# Revit family: Mailboxes_Americana-Salsbury_Industries-Rear_Loading
name_source: partatom
category: Specialty Equipment
revit_build: Autodesk Revit 2016 (Build: 20150714_1515(x64)
units: mm (PartAtom-declared; Revit-internal decimal feet)

## family parameters
Always vertical = Yes
Cut with Voids When Loaded = No
OmniClass Number = 23.40.90.14.11
OmniClass Title = Mail Boxes
Part Type = Normal
Room Calculation Point = No
Round Connector Dimension = Use Diameter
Shared = No
Work Plane-Based = No

## types (4) — shared parameters
Assembly Code = C1030910
Depth = 14.875 "
Door Material = Brass Die Cast - Salsbury Finish - Brass
Door Material - Textured = Brass Die Cast - Salsbury Finish - Textured
Door Window Material = Glass - Salsbury Finish - Clear
Enclosure Material = Steel - Salsbury Finish - Tan
Height = 26.375 "
Lock Material = Stainless Steel - Salsbury Finish - Gold
Manufacturer = Salsbury Industries
MasterFormat Number = 10 55 00
MasterFormat Title = Postal Specialties
Name Plate Material = Aluminum - Salsbury Finish -  Brushed Steel
Name Plate Offset = 0.032 "
OmniClass 23 Title = Mail Boxes
OmniClass23 Number = 23.40.90.14.11
Type Comments = Brass Mailbox for Private Delivery
URL = www.mailboxes.com
Version = 2.0 (05/31/18)
Width = 23.5 "
zero-valued in all types: Door Offset for Front Loading Units

## per-type parameters (varying)
- 2016RL: Description=Rear-Loading Unit with 16 #2 Doors; Divider 6 and 7 Offset=0 "; Door Slot L1=Brass Mailbox No Door : Empty; Door Slot L1-A=Brass Mailbox #2 Door : #2 Door; Door Slot L10=Brass Mailbox No Door : Empty; Door Slot L10-A=Brass Mailbox #2 Door : #2 Door; Door Slot L11=Brass Mailbox No Door : Empty; Door Slot L11-A=Brass Mailbox #2 Door : #2 Door; Door Slot L12=Brass Mailbox No Door : Empty; Door Slot L12-A=Brass Mailbox #2 Door : #2 Door; Door Slot L13=Brass Mailbox No Door : Empty; Door Slot L13-A=Brass Mailbox #2 Door : #2 Door; Door Slot L14=Brass Mailbox No Door : Empty; Door Slot L14-A=Brass Mailbox #2 Door : #2 Door; Door Slot L15=Brass Mailbox No Door : Empty; Door Slot L15-A=Brass Mailbox #2 Door : #2 Door; Door Slot L16=Brass Mailbox No Door : Empty; Door Slot L16-A=Brass Mailbox #2 Door : #2 Door; Door Slot L17=Brass Mailbox No Door : Empty; Door Slot L18=Brass Mailbox No Door : Empty; Door Slot L19=Brass Mailbox No Door : Empty; Door Slot L2=Brass Mailbox No Door : Empty; Door Slot L2-A=Brass Mailbox #2 Door : #2 Door; Door Slot L20=Brass Mailbox No Door : Empty; Door Slot L21=Brass Mailbox No Door : Empty; Door Slot L22=Brass Mailbox No Door : Empty; Door Slot L23=Brass Mailbox No Door : Empty; Door Slot L24=Brass Mailbox No Door : Empty; Door Slot L25=Brass Mailbox No Door : Empty; Door Slot L26=Brass Mailbox No Door : Empty; Door Slot L27=Brass Mailbox No Door : Empty; Door Slot L28=Brass Mailbox No Door : Empty; Door Slot L29=Brass Mailbox No Door : Empty; Door Slot L3=Brass Mailbox No Door : Empty; Door Slot L3-A=Brass Mailbox #2 Door : #2 Door; Door Slot L30=Brass Mailbox No Door : Empty; Door Slot L4=Brass Mailbox No Door : Empty; Door Slot L4-A=Brass Mailbox #2 Door : #2 Door; Door Slot L5=Brass Mailbox No Door : Empty; Door Slot L5-A=Brass Mailbox #2 Door : #2 Door; Door Slot L6=Brass Mailbox No Door : Empty; Door Slot L6-A=Brass Mailbox #2 Door : #2 Door; Door Slot L7=Brass Mailbox No Door : Empty; Door Slot L7-A=Brass Mailbox #2 Door : #2 Door; Door Slot L8=Brass Mailbox No Door : Empty; Door Slot L8-A=Brass Mailbox #2 Door : #2 Door; Door Slot L9=Brass Mailbox No Door : Empty; Door Slot L9-A=Brass Mailbox #2 Door : #2 Door; Horizontal Dividers 1, 2, 3, 4=No; Horizontal Dividers 5, 6, 7=Yes; Vertical Dividers 1, 2, 4, 5=No; Vertical Dividers 6, 7=Yes
- 2030RL: Description=Rear-Loading Unit with 30 #1 Doors; Divider 6 and 7 Offset=0 "; Door Slot L1=Brass Mailbox #1 Door : #1 Door; Door Slot L1-A=Brass Mailbox No Door : Empty; Door Slot L10=Brass Mailbox #1 Door : #1 Door; Door Slot L10-A=Brass Mailbox No Door : Empty; Door Slot L11=Brass Mailbox #1 Door : #1 Door; Door Slot L11-A=Brass Mailbox No Door : Empty; Door Slot L12=Brass Mailbox #1 Door : #1 Door; Door Slot L12-A=Brass Mailbox No Door : Empty; Door Slot L13=Brass Mailbox #1 Door : #1 Door; Door Slot L13-A=Brass Mailbox No Door : Empty; Door Slot L14=Brass Mailbox #1 Door : #1 Door; Door Slot L14-A=Brass Mailbox No Door : Empty; Door Slot L15=Brass Mailbox #1 Door : #1 Door; Door Slot L15-A=Brass Mailbox No Door : Empty; Door Slot L16=Brass Mailbox #1 Door : #1 Door; Door Slot L16-A=Brass Mailbox No Door : Empty; Door Slot L17=Brass Mailbox #1 Door : #1 Door; Door Slot L18=Brass Mailbox #1 Door : #1 Door; Door Slot L19=Brass Mailbox #1 Door : #1 Door; Door Slot L2=Brass Mailbox #1 Door : #1 Door; Door Slot L2-A=Brass Mailbox No Door : Empty; Door Slot L20=Brass Mailbox #1 Door : #1 Door; Door Slot L21=Brass Mailbox #1 Door : #1 Door; Door Slot L22=Brass Mailbox #1 Door : #1 Door; Door Slot L23=Brass Mailbox #1 Door : #1 Door; Door Slot L24=Brass Mailbox #1 Door : #1 Door; Door Slot L25=Brass Mailbox #1 Door : #1 Door; Door Slot L26=Brass Mailbox #1 Door : #1 Door; Door Slot L27=Brass Mailbox #1 Door : #1 Door; Door Slot L28=Brass Mailbox #1 Door : #1 Door; Door Slot L29=Brass Mailbox #1 Door : #1 Door; Door Slot L3=Brass Mailbox #1 Door : #1 Door; Door Slot L3-A=Brass Mailbox No Door : Empty; Door Slot L30=Brass Mailbox #1 Door : #1 Door; Door Slot L4=Brass Mailbox #1 Door : #1 Door; Door Slot L4-A=Brass Mailbox No Door : Empty; Door Slot L5=Brass Mailbox #1 Door : #1 Door; Door Slot L5-A=Brass Mailbox No Door : Empty; Door Slot L6=Brass Mailbox #1 Door : #1 Door; Door Slot L6-A=Brass Mailbox No Door : Empty; Door Slot L7=Brass Mailbox #1 Door : #1 Door; Door Slot L7-A=Brass Mailbox No Door : Empty; Door Slot L8=Brass Mailbox #1 Door : #1 Door; Door Slot L8-A=Brass Mailbox No Door : Empty; Door Slot L9=Brass Mailbox #1 Door : #1 Door; Door Slot L9-A=Brass Mailbox No Door : Empty; Horizontal Dividers 1, 2, 3, 4=Yes; Horizontal Dividers 5, 6, 7=No; Vertical Dividers 1, 2, 4, 5=Yes; Vertical Dividers 6, 7=No
- 2014RL: Description=Rear-Loading Unit with 14 #2 Doors, 2 #3 Doors; Divider 6 and 7 Offset=6.577 "; Door Slot L1=Brass Mailbox No Door : Empty; Door Slot L1-A=Brass Mailbox #2 Door : #2 Door; Door Slot L10=Brass Mailbox No Door : Empty; Door Slot L10-A=Brass Mailbox #2 Door : #2 Door; Door Slot L11=Brass Mailbox No Door : Empty; Door Slot L11-A=Brass Mailbox #2 Door : #2 Door; Door Slot L12=Brass Mailbox No Door : Empty; Door Slot L12-A=Brass Mailbox #2 Door : #2 Door; Door Slot L13=Brass Mailbox No Door : Empty; Door Slot L13-A=Brass Mailbox No Door : Empty; Door Slot L14=Brass Mailbox No Door : Empty; Door Slot L14-A=Brass Mailbox #3 Door : #3 Door; Door Slot L15=Brass Mailbox No Door : Empty; Door Slot L15-A=Brass Mailbox No Door : Empty; Door Slot L16=Brass Mailbox No Door : Empty; Door Slot L16-A=Brass Mailbox #3 Door : #3 Door; Door Slot L17=Brass Mailbox No Door : Empty; Door Slot L18=Brass Mailbox No Door : Empty; Door Slot L19=Brass Mailbox No Door : Empty; Door Slot L2=Brass Mailbox No Door : Empty; Door Slot L2-A=Brass Mailbox #2 Door : #2 Door; Door Slot L20=Brass Mailbox No Door : Empty; Door Slot L21=Brass Mailbox No Door : Empty; Door Slot L22=Brass Mailbox No Door : Empty; Door Slot L23=Brass Mailbox No Door : Empty; Door Slot L24=Brass Mailbox No Door : Empty; Door Slot L25=Brass Mailbox No Door : Empty; Door Slot L26=Brass Mailbox No Door : Empty; Door Slot L27=Brass Mailbox No Door : Empty; Door Slot L28=Brass Mailbox No Door : Empty; Door Slot L29=Brass Mailbox No Door : Empty; Door Slot L3=Brass Mailbox No Door : Empty; Door Slot L3-A=Brass Mailbox #2 Door : #2 Door; Door Slot L30=Brass Mailbox No Door : Empty; Door Slot L4=Brass Mailbox No Door : Empty; Door Slot L4-A=Brass Mailbox #2 Door : #2 Door; Door Slot L5=Brass Mailbox No Door : Empty; Door Slot L5-A=Brass Mailbox #2 Door : #2 Door; Door Slot L6=Brass Mailbox No Door : Empty; Door Slot L6-A=Brass Mailbox #2 Door : #2 Door; Door Slot L7=Brass Mailbox No Door : Empty; Door Slot L7-A=Brass Mailbox #2 Door : #2 Door; Door Slot L8=Brass Mailbox No Door : Empty; Door Slot L8-A=Brass Mailbox #2 Door : #2 Door; Door Slot L9=Brass Mailbox No Door : Empty; Door Slot L9-A=Brass Mailbox #2 Door : #2 Door; Horizontal Dividers 1, 2, 3, 4=No; Horizontal Dividers 5, 6, 7=Yes; Vertical Dividers 1, 2, 4, 5=No; Vertical Dividers 6, 7=Yes
- 2008RL: Description=Rear-Loading Unit with 8 #3 Doors; Divider 6 and 7 Offset=0 "; Door Slot L1=Brass Mailbox No Door : Empty; Door Slot L1-A=Brass Mailbox No Door : Empty; Door Slot L10=Brass Mailbox No Door : Empty; Door Slot L10-A=Brass Mailbox #3 Door : #3 Door; Door Slot L11=Brass Mailbox No Door : Empty; Door Slot L11-A=Brass Mailbox No Door : Empty; Door Slot L12=Brass Mailbox No Door : Empty; Door Slot L12-A=Brass Mailbox #3 Door : #3 Door; Door Slot L13=Brass Mailbox No Door : Empty; Door Slot L13-A=Brass Mailbox No Door : Empty; Door Slot L14=Brass Mailbox No Door : Empty; Door Slot L14-A=Brass Mailbox #3 Door : #3 Door; Door Slot L15=Brass Mailbox No Door : Empty; Door Slot L15-A=Brass Mailbox No Door : Empty; Door Slot L16=Brass Mailbox No Door : Empty; Door Slot L16-A=Brass Mailbox #3 Door : #3 Door; Door Slot L17=Brass Mailbox No Door : Empty; Door Slot L18=Brass Mailbox No Door : Empty; Door Slot L19=Brass Mailbox No Door : Empty; Door Slot L2=Brass Mailbox No Door : Empty; Door Slot L2-A=Brass Mailbox #3 Door : #3 Door; Door Slot L20=Brass Mailbox No Door : Empty; Door Slot L21=Brass Mailbox No Door : Empty; Door Slot L22=Brass Mailbox No Door : Empty; Door Slot L23=Brass Mailbox No Door : Empty; Door Slot L24=Brass Mailbox No Door : Empty; Door Slot L25=Brass Mailbox No Door : Empty; Door Slot L26=Brass Mailbox No Door : Empty; Door Slot L27=Brass Mailbox No Door : Empty; Door Slot L28=Brass Mailbox No Door : Empty; Door Slot L29=Brass Mailbox No Door : Empty; Door Slot L3=Brass Mailbox No Door : Empty; Door Slot L3-A=Brass Mailbox No Door : Empty; Door Slot L30=Brass Mailbox No Door : Empty; Door Slot L4=Brass Mailbox No Door : Empty; Door Slot L4-A=Brass Mailbox #3 Door : #3 Door; Door Slot L5=Brass Mailbox No Door : Empty; Door Slot L5-A=Brass Mailbox No Door : Empty; Door Slot L6=Brass Mailbox No Door : Empty; Door Slot L6-A=Brass Mailbox #3 Door : #3 Door; Door Slot L7=Brass Mailbox No Door : Empty; Door Slot L7-A=Brass Mailbox No Door : Empty; Door Slot L8=Brass Mailbox No Door : Empty; Door Slot L8-A=Brass Mailbox #3 Door : #3 Door; Door Slot L9=Brass Mailbox No Door : Empty; Door Slot L9-A=Brass Mailbox No Door : Empty; Horizontal Dividers 1, 2, 3, 4=No; Horizontal Dividers 5, 6, 7=Yes; Vertical Dividers 1, 2, 4, 5=No; Vertical Dividers 6, 7=No

note: column(s) folded — value = type name in every type: Model

## geometry (parser evidence)
native form markers: Sweep x11
no freeform markers — native parametric forms only
